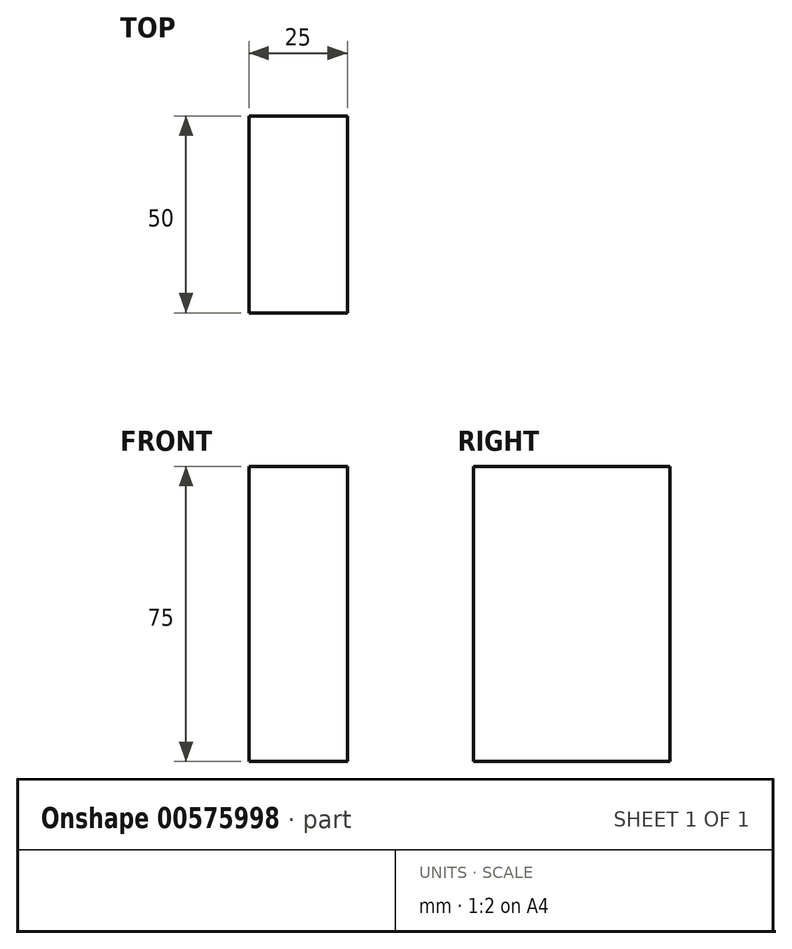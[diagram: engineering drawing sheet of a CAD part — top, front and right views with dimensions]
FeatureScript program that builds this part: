
annotation { "Feature Type Name" : "Feature", "Feature Type Description" : "" }
export const myFeature = defineFeature(function(context is Context, id is Id, definition is map)
    precondition{}
    {
        {
            var Q0;
            Q0=qCreatedBy(makeId("Top.planeOp"),FACE);
            var sketch = newSketch(context, id + "F0", { "sketchPlane" : qUnion([Q0])});
            skLineSegment(sketch, "E0.bottom", {"start": v(36.65, 2.02) * mm, "end": v(61.65, 2.02) * mm});
            skLineSegment(sketch, "E0.top", {"start": v(36.65, -47.98) * mm, "end": v(61.65, -47.98) * mm});
            skLineSegment(sketch, "E0.left", {"start": v(36.65, 2.02) * mm, "end": v(36.65, -47.98) * mm});
            skLineSegment(sketch, "E0.right", {"start": v(61.65, 2.02) * mm, "end": v(61.65, -47.98) * mm});
            skSolve(sketch);
        }
        {
            var Q0;
            Q0=makeQuery(id+"F0.imprint","IMPRINT",FACE,{"disambiguationData":[TD([[makeQuery(id+"F0.imprint","IMPRINT",EDGE,{"derivedFrom":sQuery(id+"F0.wireOp",EDGE,"E0.bottom")}),-1.0]])]});
            extrude(context, id + "F1", {"entities" : qUnion([Q0]), "depth" : 75 * mm, "offsetDistance" : 25 * mm});
        }
    });
